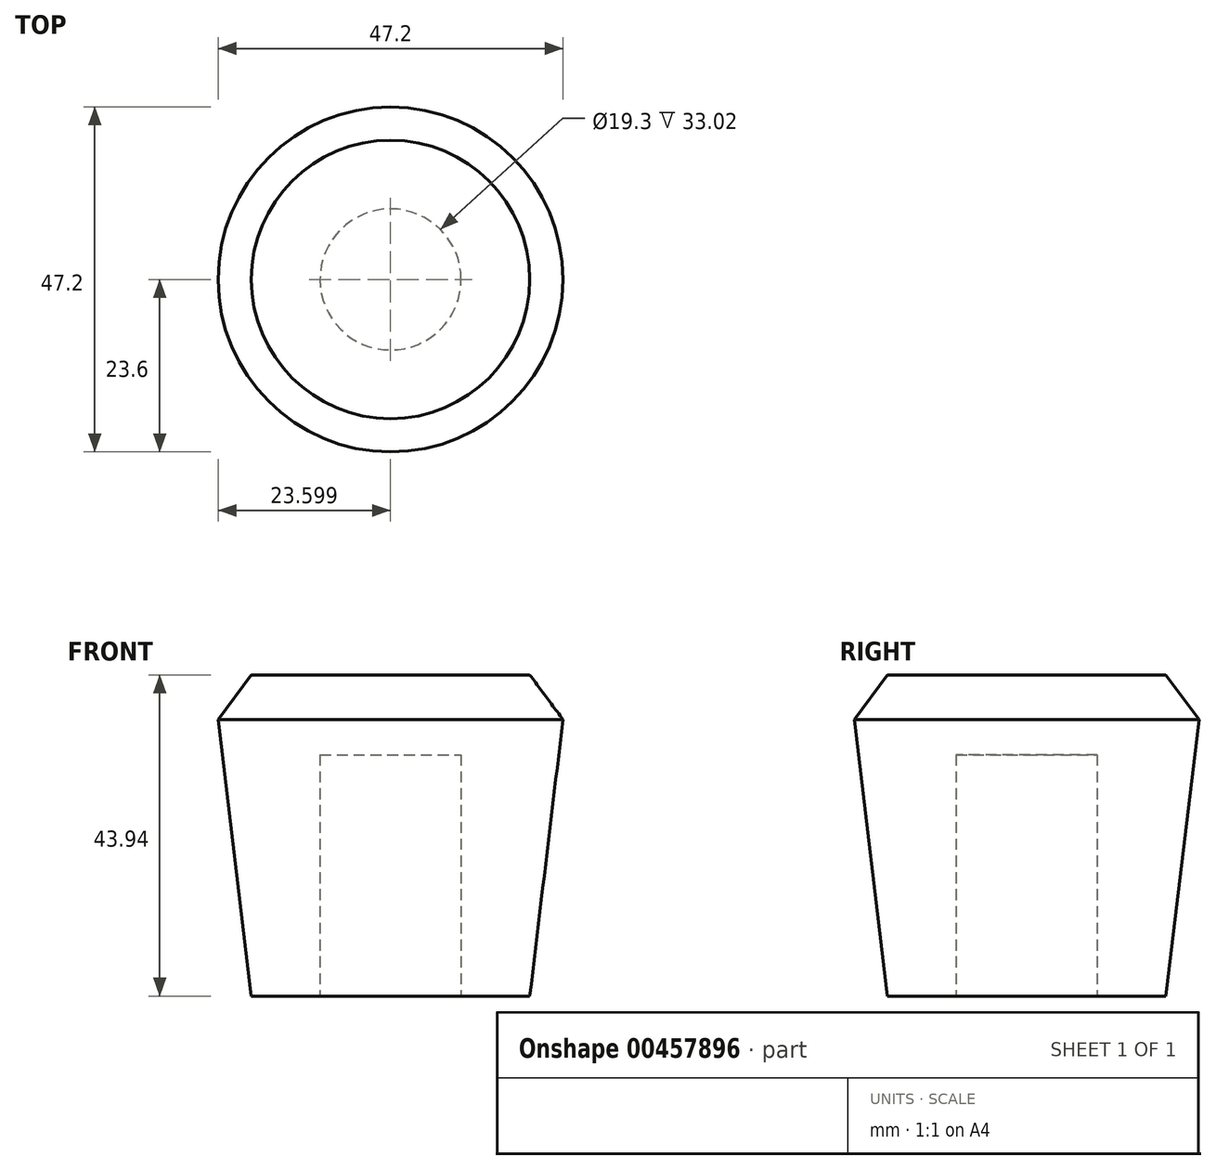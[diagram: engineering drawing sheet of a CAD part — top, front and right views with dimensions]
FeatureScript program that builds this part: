
annotation { "Feature Type Name" : "Feature", "Feature Type Description" : "" }
export const myFeature = defineFeature(function(context is Context, id is Id, definition is map)
    precondition{}
    {
        {
            var Q0;
            Q0=qCreatedBy(makeId("Front.planeOp"),FACE);
            var sketch = newSketch(context, id + "F0", { "sketchPlane" : qUnion([Q0])});
            skLineSegment(sketch, "E0", {"start": v(-65.62, -6.8) * mm, "end": v(-46.57, -6.8) * mm});
            skLineSegment(sketch, "E1", {"start": v(-46.57, 37.14) * mm, "end": v(-65.62, 37.14) * mm});
            skLineSegment(sketch, "E2", {"start": v(-65.62, 37.14) * mm, "end": v(-70.17, 31.02) * mm});
            skLineSegment(sketch, "E3", {"start": v(-70.17, 31.02) * mm, "end": v(-65.62, -6.8) * mm});
            skLineSegment(sketch, "E4", {"start": v(-46.57, 37.14) * mm, "end": v(-46.57, -6.8) * mm});
            skSolve(sketch);
        }
        {
            var Q0;
            Q0 = qSketchRegion(id + "F2", true);
            var Q1;
            Q1=makeQuery(id+"F0.imprint","IMPRINT",FACE,{"disambiguationData":[TD([[makeQuery(id+"F0.imprint","IMPRINT",EDGE,{"derivedFrom":sQuery(id+"F0.wireOp",EDGE,"E0")}),1.0]])]});
            var Q2;
            Q2=sQuery(id+"F0.wireOp",EDGE,"E4");
            revolve(context, id + "F1", {"entities" : qUnion([Q0, Q1]), "axis" : qUnion([Q2]), "revolveType" : RevolveType.FULL});
        }
        {
            var Q0;
            Q0=makeQuery(id+"F1.opRevolve","SWEPT_FACE",FACE,{"disambiguationData":[OSD([sQuery(id+"F0.wireOp",EDGE,"E0")])]});
            var sketch = newSketch(context, id + "F2", { "sketchPlane" : qUnion([Q0])});
            skLineSegment(sketch, "E5", {"start": v(-65.62, 0) * mm, "end": v(-27.52, 0) * mm, "construction": true});
            skCircle(sketch, "E6", {"center": v(-46.57, 0) * mm, "radius": 9.65 * mm});
            skSolve(sketch);
        }
        {
            var Q0;
            Q0 = qSketchRegion(id + "F2", true);
            extrude(context, id + "F3", {"entities" : qUnion([Q0]), "operationType" : NewBodyOperationType.REMOVE, "oppositeDirection" : true, "depth" : 33.02 * mm});
        }
    });
